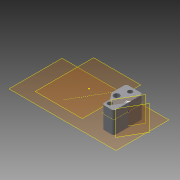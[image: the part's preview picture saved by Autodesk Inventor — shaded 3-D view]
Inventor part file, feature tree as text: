
AUTODESK INVENTOR PART (.ipt)
format: ipt  version: 2015 (Build 190159000, 159)  size: 122,880 bytes
history: native  units: mm
features: plane x5, reference x4, sketch x3, extrude x1, hole x1, fillet x1, projected_geometry x1
ambient origin geometry x8: Origin, YZ Plane, XZ Plane, XY Plane, X Axis, Y Axis, Z Axis, Center Point
bodies: Solid1 (feature_tree)
feature tree (16):
  plane  "Work Plane1"
  plane  "Work Plane2"
  sketch  "Sketch1"  dims[d1=3.0mm d2=10.0mm d3=0.0mm]
  extrude  "Extrusion1"  Depth=10.0mm TaperAngle=0.0deg
  plane  "Work Plane4"
  sketch  "Sketch4"  dims[d6=4.0mm d16=10.0mm]
  plane  "Work Plane8"
  hole  "Hole2"  [1 undecoded]
  fillet  "Fillet1"  Radius=2.0mm
  reference  "Reference3"
  reference  "Reference4"
  reference  "Reference11"
  projected_geometry  "Projected Loop1"
  reference  "Reference12"
  plane  "Work Plane7"
  sketch  "Sketch7"  dims[d17=2.459mm d18=6.0mm d19=4.0mm d20=2.0mm d21=90.0deg d22=8.0mm d23=20.594885mm d24=2.0mm d26=26.0mm d29=7.0mm]
note: 1 required parameter value undecoded (feature->parameter linkage not recoverable at this tier; creation-order binding heuristic only, values carry confidence <= 0.55)
